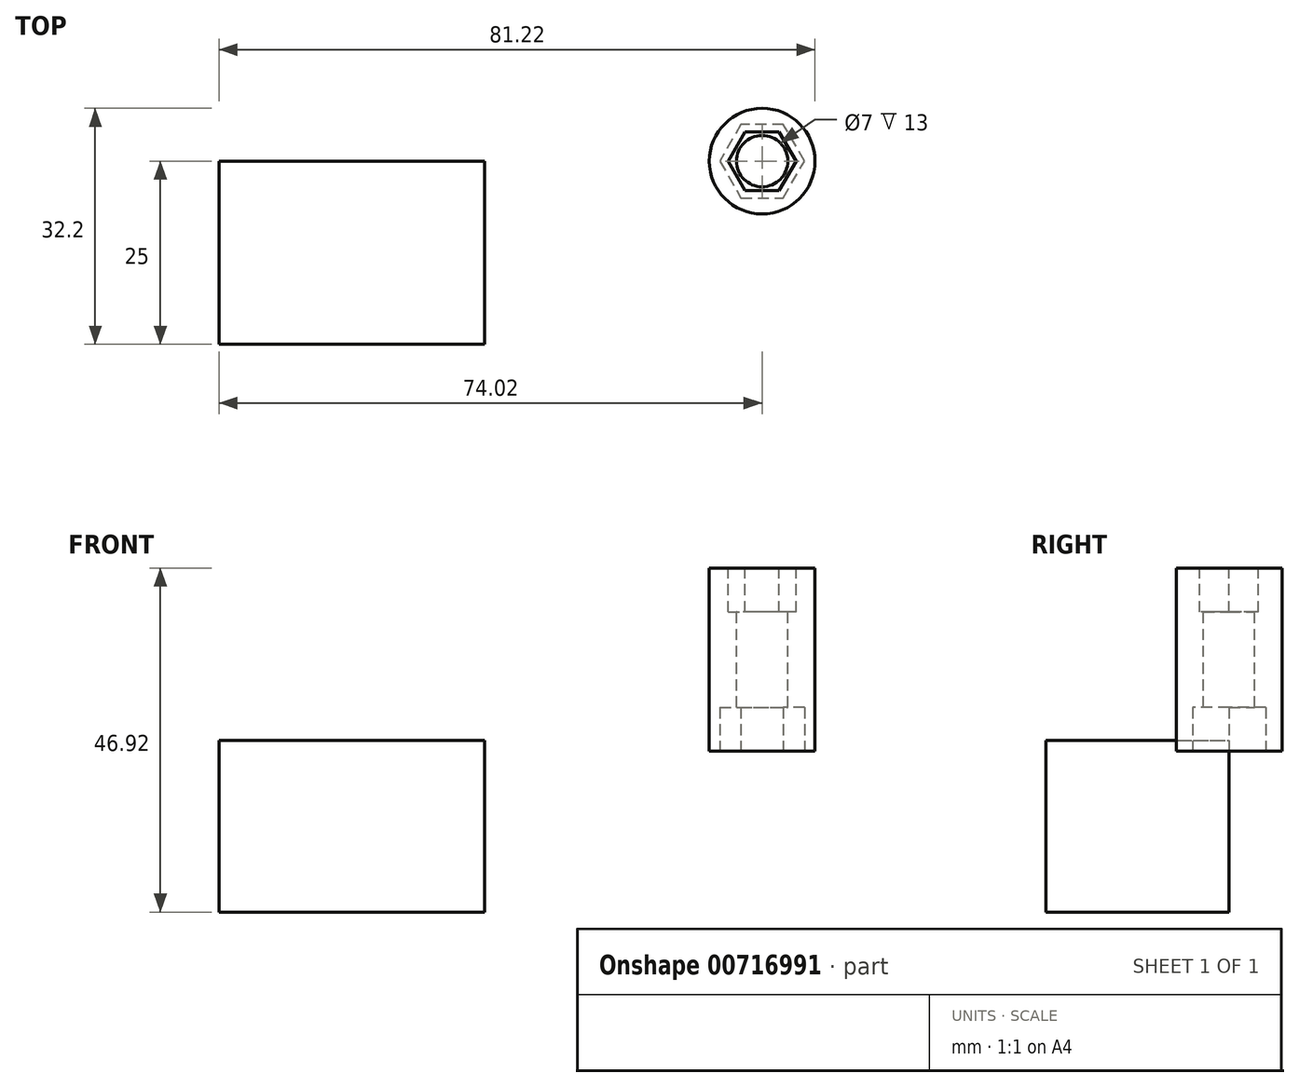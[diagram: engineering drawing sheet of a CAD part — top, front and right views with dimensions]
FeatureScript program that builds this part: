
annotation { "Feature Type Name" : "Feature", "Feature Type Description" : "" }
export const myFeature = defineFeature(function(context is Context, id is Id, definition is map)
    precondition{}
    {
        {
            var Q0;
            Q0=qCreatedBy(makeId("Top.planeOp"),FACE);
            var sketch = newSketch(context, id + "F0", { "sketchPlane" : qUnion([Q0])});
            skCircle(sketch, "E0", {"center": v(0, 0) * mm, "radius": 7.2 * mm});
            skSolve(sketch);
        }
        {
            var Q0;
            Q0=makeQuery(id+"F0.imprint","IMPRINT",FACE,{"disambiguationData":[TD([[makeQuery(id+"F0.imprint","IMPRINT",EDGE,{"derivedFrom":sQuery(id+"F0.wireOp",EDGE,"E0")}),1.0]])]});
            extrude(context, id + "F1", {"entities" : qUnion([Q0]), "oppositeDirection" : true, "depth" : 25 * mm, "offsetDistance" : 25 * mm});
        }
        {
            var Q0;
            Q0=makeQuery(id+"F1.opExtrude","CAP_FACE",FACE,{"disambiguationData":[OSD([sQuery(id+"F0.wireOp",EDGE,"E0")])],"isStart":true});
            var sketch = newSketch(context, id + "F2", { "sketchPlane" : qUnion([Q0])});
            skCircle(sketch, "E1.cCircle", {"center": v(0, 0) * mm, "radius": 4 * mm, "construction": true});
            skLineSegment(sketch, "E1.0", {"start": v(2.3, -4) * mm, "end": v(-2.3, -4) * mm});
            skLineSegment(sketch, "E1.1", {"start": v(-2.3, -4) * mm, "end": v(-4.62, 0) * mm});
            skLineSegment(sketch, "E1.2", {"start": v(-4.62, 0) * mm, "end": v(-2.3, 4) * mm});
            skLineSegment(sketch, "E1.3", {"start": v(-2.3, 4) * mm, "end": v(2.3, 4) * mm});
            skLineSegment(sketch, "E1.4", {"start": v(2.3, 4) * mm, "end": v(4.62, 0) * mm});
            skLineSegment(sketch, "E1.5", {"start": v(4.62, 0) * mm, "end": v(2.3, -4) * mm});
            skPoint(sketch, "E1.0.midPoint", {"position": v(0, -4) * mm});
            skSolve(sketch);
        }
        {
            var Q0;
            Q0 = qSketchRegion(id + "F2", true);
            extrude(context, id + "F3", {"entities" : qUnion([Q0]), "operationType" : NewBodyOperationType.REMOVE, "oppositeDirection" : true, "depth" : 6 * mm, "offsetDistance" : 25 * mm});
        }
        {
            var Q0;
            Q0=makeQuery(id+"F1.opExtrude","CAP_FACE",FACE,{"disambiguationData":[OSD([sQuery(id+"F0.wireOp",EDGE,"E0")])],"isStart":false});
            var sketch = newSketch(context, id + "F4", { "sketchPlane" : qUnion([Q0])});
            skSolve(sketch);
        }
        {
            var Q0;
            Q0=makeQuery(id+"F4.imprint","IMPRINT",FACE,{"disambiguationData":[TD([[makeQuery(id+"F4.imprint","IMPRINT",EDGE,{"derivedFrom":makeQuery(id+"F1.opExtrude","CAP_EDGE",EDGE,{"disambiguationData":[OSD([sQuery(id+"F0.wireOp",EDGE,"E0")])],"isStart":false})}),-1.0]])]});
            var sketch = newSketch(context, id + "F5", { "sketchPlane" : qUnion([Q0])});
            skCircle(sketch, "E2.cCircle", {"center": v(0, 0) * mm, "radius": 5 * mm, "construction": true});
            skLineSegment(sketch, "E2.0", {"start": v(-2.89, 5) * mm, "end": v(2.89, 5) * mm});
            skLineSegment(sketch, "E2.1", {"start": v(2.89, 5) * mm, "end": v(5.77, 0) * mm});
            skLineSegment(sketch, "E2.2", {"start": v(5.77, 0) * mm, "end": v(2.89, -5) * mm});
            skLineSegment(sketch, "E2.3", {"start": v(2.89, -5) * mm, "end": v(-2.89, -5) * mm});
            skLineSegment(sketch, "E2.4", {"start": v(-2.89, -5) * mm, "end": v(-5.77, 0) * mm});
            skLineSegment(sketch, "E2.5", {"start": v(-5.77, 0) * mm, "end": v(-2.89, 5) * mm});
            skPoint(sketch, "E2.0.midPoint", {"position": v(0, 5) * mm});
            skSolve(sketch);
        }
        {
            var Q0;
            Q0=makeQuery(id+"F5.imprint","IMPRINT",FACE,{"disambiguationData":[TD([[makeQuery(id+"F5.imprint","IMPRINT",EDGE,{"derivedFrom":sQuery(id+"F5.wireOp",EDGE,"E2.0")}),-1.0]])]});
            extrude(context, id + "F6", {"entities" : qUnion([Q0]), "operationType" : NewBodyOperationType.REMOVE, "oppositeDirection" : true, "depth" : 6 * mm, "offsetDistance" : 25 * mm});
        }
        {
            var Q0;
            Q0=qCreatedBy(makeId("Top.planeOp"),FACE);
            var sketch = newSketch(context, id + "F7", { "sketchPlane" : qUnion([Q0])});
            skCircle(sketch, "E3", {"center": v(0, 0) * mm, "radius": 3.5 * mm});
            skSolve(sketch);
        }
        {
            var Q0;
            Q0 = qSketchRegion(id + "F7", true);
            extrude(context, id + "F8", {"entities" : qUnion([Q0]), "operationType" : NewBodyOperationType.REMOVE, "oppositeDirection" : true, "depth" : 25 * mm, "offsetDistance" : 25 * mm});
        }
        {
            var Q0;
            Q0=qCreatedBy(makeId("Front.planeOp"),FACE);
            var sketch = newSketch(context, id + "F9", { "sketchPlane" : qUnion([Q0])});
            skLineSegment(sketch, "E4.bottom", {"start": v(-74.02, -23.52) * mm, "end": v(-37.85, -23.52) * mm});
            skLineSegment(sketch, "E4.top", {"start": v(-74.02, -46.92) * mm, "end": v(-37.85, -46.92) * mm});
            skLineSegment(sketch, "E4.left", {"start": v(-74.02, -23.52) * mm, "end": v(-74.02, -46.92) * mm});
            skLineSegment(sketch, "E4.right", {"start": v(-37.85, -23.52) * mm, "end": v(-37.85, -46.92) * mm});
            skSolve(sketch);
        }
        {
            var Q0;
            Q0=makeQuery(id+"F9.imprint","IMPRINT",FACE,{"disambiguationData":[TD([[makeQuery(id+"F9.imprint","IMPRINT",EDGE,{"derivedFrom":sQuery(id+"F9.wireOp",EDGE,"E4.bottom")}),-1.0]])]});
            extrude(context, id + "F10", {"entities" : qUnion([Q0]), "depth" : 25 * mm, "offsetDistance" : 25 * mm});
        }
    });
